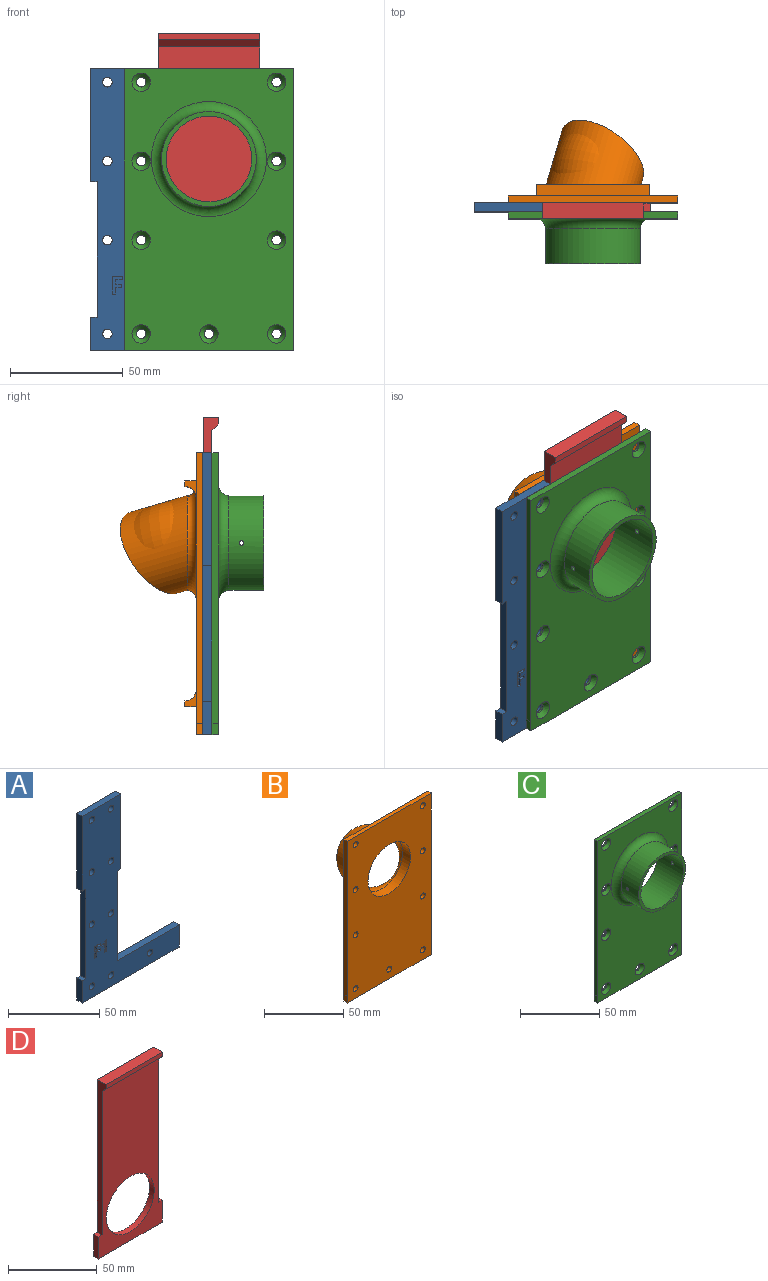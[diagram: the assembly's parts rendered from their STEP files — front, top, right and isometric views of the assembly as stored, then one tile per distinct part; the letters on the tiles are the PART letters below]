
ASSEMBLY  parts=4 mates=3
PART A: 45 faces, bbox 75x4x125 mm
  f0: plane 125x75mm, normal (0,-1,0), area 3900.4mm2, adj f1,f2,f3,f4,f5,f6,f7,f8
  f1: plane 30x4mm, normal (0,0,1), area 120mm2, adj f0,f2,f12,f17
  f2: plane 50.1x4mm, normal (-1,0,0), area 200.4mm2, adj f0,f1,f3,f12
  f3: plane 4x3mm, normal (0,0,-1), area 12mm2, adj f0,f2,f4,f12
  f4: plane 60x4mm, normal (-1,0,0), area 240mm2, adj f0,f3,f5,f12
  f5: plane 4x3mm, normal (0,0,1), area 12mm2, adj f0,f4,f6,f12
  f6: plane 14.9x4mm, normal (-1,0,0), area 59.6mm2, adj f0,f5,f11,f12
  f7: cylinder r=2.1mm len=4.2mm, axis (0,-1,0), area 52.8mm2, adj f0,f12
  f8: cylinder r=2.1mm len=4.2mm, axis (0,-1,0), area 52.8mm2, adj f0,f12
  f9: cylinder r=2.1mm len=4.2mm, axis (0,-1,0), area 52.8mm2, adj f0,f12
  f10: cylinder r=2.1mm len=4.2mm, axis (0,-1,0), area 52.8mm2, adj f0,f12
  f11: plane 75x4mm, normal (0,0,-1), area 300mm2, adj f0,f6,f12,f13
  f12: plane 125x75mm, normal (0,1,0), area 3935.9mm2, adj f1,f2,f3,f4,f5,f6,f7,f8
  f13: plane 14.9x4mm, normal (1,0,0), area 59.6mm2, adj f0,f11,f12,f14
  f14: plane 48x4mm, normal (0,0,1), area 192mm2, adj f0,f12,f13,f15
  f15: plane 60x4mm, normal (1,0,0), area 240mm2, adj f0,f12,f14,f16
  f16: plane 4x3mm, normal (0,0,-1), area 12mm2, adj f0,f12,f15,f17
  f17: plane 50.1x4mm, normal (1,0,0), area 200.4mm2, adj f0,f1,f12,f16
  f18: cylinder r=2.1mm len=4.2mm, axis (0,-1,0), area 52.8mm2, adj f0,f12
  f19: cylinder r=2.1mm len=4.2mm, axis (0,-1,0), area 52.8mm2, adj f0,f12
  f20: cylinder r=2.1mm len=4.2mm, axis (0,-1,0), area 52.8mm2, adj f0,f12
  f21: cylinder r=2.1mm len=4.2mm, axis (0,-1,0), area 52.8mm2, adj f0,f12
  f22: cylinder r=2.1mm len=4.2mm, axis (0,-1,0), area 52.8mm2, adj f0,f12
  f23: plane 1.64x1mm, normal (0,0,1), area 1.6mm2, adj f0,f24,f32,f33
  f24: plane 7.76x1mm, normal (-1,0,0), area 7.8mm2, adj f0,f23,f25,f33
  f25: plane 1.35x1mm, normal (0,0,-1), area 1.3mm2, adj f0,f24,f26,f33
  f26: plane 2.5x1.99mm, normal (0.62,0,-0.78), area 3.2mm2, adj f0,f25,f27,f33
  f27: plane 1x0.99mm, normal (0.78,0,0.63), area 1.3mm2, adj f0,f26,f28,f33
  f28: plane 1x0.89mm, normal (-0.63,0,0.78), area 1.1mm2, adj f0,f27,f29,f33
  f29: extruded ~1x0.57mm, area 0.8mm2, adj f0,f28,f30,f33
  f30: plane 1x0.81mm, normal (1,0,-0.03), area 0.8mm2, adj f0,f29,f31,f33
  f31: plane 1x0.74mm, normal (1,0,-0.02), area 0.7mm2, adj f0,f30,f32,f33
  f32: plane 4.49x1mm, normal (1,0,0), area 4.5mm2, adj f0,f23,f31,f33
  f33: plane 7.76x3.85mm, normal (0,-1,0), area 15.6mm2, adj f23,f24,f25,f26,f27,f28,f29,f30
  f34: plane 1.62x1mm, normal (0,0,1), area 1.6mm2, adj f0,f35,f43,f44
  f35: plane 3.07x1mm, normal (-1,0,0), area 3.1mm2, adj f0,f34,f36,f44
  f36: plane 2.63x1mm, normal (0,0,1), area 2.6mm2, adj f0,f35,f37,f44
  f37: plane 1.34x1mm, normal (-1,0,0), area 1.3mm2, adj f0,f36,f38,f44
  f38: plane 2.63x1mm, normal (0,0,-1), area 2.6mm2, adj f0,f37,f39,f44
  f39: plane 2x1mm, normal (-1,0,0), area 2mm2, adj f0,f38,f40,f44
  f40: plane 2.83x1mm, normal (0,0,1), area 2.8mm2, adj f0,f39,f41,f44
  f41: plane 1.35x1mm, normal (-1,0,0), area 1.3mm2, adj f0,f40,f42,f44
  f42: plane 4.45x1mm, normal (0,0,-1), area 4.4mm2, adj f0,f41,f43,f44
  f43: plane 7.76x1mm, normal (1,0,0), area 7.8mm2, adj f0,f34,f42,f44
  f44: plane 7.76x4.45mm, normal (0,-1,0), area 19.9mm2, adj f34,f35,f36,f37,f38,f39,f40,f41
PART B: 35 faces, bbox 75x39.1x125 mm
  f0: plane 125x75mm, normal (0,1,0), area 6638.9mm2, adj f1,f2,f3,f4,f5,f6,f7,f8
  f1: plane 125x3mm, normal (1,0,0), area 375mm2, adj f0,f2,f13,f15
  f2: plane 75x3mm, normal (0,0,1), area 225mm2, adj f0,f1,f3,f15
  f3: plane 120x3mm, normal (-1,0,0), area 360mm2, adj f0,f2,f4,f15
  f4: plane 5x3mm, normal (-1,0,0), area 15mm2, adj f0,f3,f13,f15
  f5: cylinder r=2.1mm len=4.2mm, axis (0,-1,0), area 39.6mm2, adj f0,f15
  f6: cylinder r=2.1mm len=4.2mm, axis (0,-1,0), area 39.6mm2, adj f0,f15
  f7: cylinder r=2.1mm len=4.2mm, axis (0,-1,0), area 39.6mm2, adj f0,f15
  f8: cylinder r=2.1mm len=4.2mm, axis (0,-1,0), area 39.6mm2, adj f0,f15
  f9: cylinder r=2.1mm len=4.2mm, axis (0,-1,0), area 39.6mm2, adj f0,f15
  f10: cylinder r=2.1mm len=4.2mm, axis (0,-1,0), area 39.6mm2, adj f0,f15
  f11: cylinder r=2.1mm len=4.2mm, axis (0,-1,0), area 39.6mm2, adj f0,f15
  f12: cylinder r=2.1mm len=4.2mm, axis (0,-1,0), area 39.6mm2, adj f0,f15
  f13: plane 75x3mm, normal (0,0,-1), area 225mm2, adj f0,f1,f4,f15
  f14: cylinder r=2.1mm len=4.2mm, axis (0,-1,0), area 39.6mm2, adj f0,f15
  f15: plane 125x75mm, normal (0,-1,0), area 8116.1mm2, adj f1,f2,f3,f4,f5,f6,f7,f8
  f16: cylinder r=19mm len=38mm, axis (0,-1,0), area 835.7mm2, adj f15,f18
  f17: torus R=21mm, axis (0.71,0,0.71), area 2176.2mm2, adj f19,f29
  f18: torus R=21mm, axis (0.71,0,0.71), area 1969mm2, adj f16,f19
  f19: plane 36.37x36.37mm, normal (0.5,0.71,-0.5), area 251.3mm2, adj f17,f18
  f20: plane 7.5x5mm, normal (1,0,0), area 17.9mm2, adj f0,f23,f24,f30
  f21: plane 30.01x5mm, normal (0,0,-1), area 56.4mm2, adj f24,f31,f33
  f22: plane 7.5x5mm, normal (-1,0,0), area 17.9mm2, adj f0,f23,f24,f34
  f23: plane 50x5mm, normal (0,0,1), area 250mm2, adj f0,f20,f22,f24
  f24: plane 50x2.5mm, normal (0,1,0), area 125mm2, adj f20,f21,f22,f23,f30,f34
  f25: plane 7.5x5mm, normal (1,0,0), area 17.9mm2, adj f0,f26,f28,f32
  f26: plane 50x5mm, normal (0,0,-1), area 250mm2, adj f0,f25,f27,f28
  f27: plane 7.5x5mm, normal (-1,0,0), area 17.9mm2, adj f0,f26,f28,f32
  f28: plane 50x2.5mm, normal (0,1,0), area 125mm2, adj f25,f26,f27,f32
  f29: torus R=25mm, axis (0,-1,0), area 886.4mm2, adj f0,f17,f31,f33
  f30: cylinder r=5mm len=10mm, axis (1,0,0), area 78.5mm2, adj f0,f20,f24,f31
  f31: bspline ~15.34x5.19mm, area 56.4mm2, adj f21,f29,f30
  f32: cylinder r=5mm len=50mm, axis (-1,0,0), area 392.7mm2, adj f0,f25,f27,f28
  f33: bspline ~15.34x5.19mm, area 56.4mm2, adj f21,f29,f34
  f34: cylinder r=5mm len=10mm, axis (1,0,0), area 78.5mm2, adj f0,f22,f24,f33
PART C: 31 faces, bbox 75x23x125 mm
  f0: plane 125x3mm, normal (1,0,0), area 375mm2, adj f1,f13,f15,f16
  f1: plane 75x3mm, normal (0,0,1), area 225mm2, adj f0,f2,f15,f16
  f2: plane 120x3mm, normal (-1,0,0), area 360mm2, adj f1,f3,f15,f16
  f3: plane 5x3mm, normal (-1,0,0), area 15mm2, adj f2,f13,f15,f16
  f4: cylinder r=2.1mm len=4.2mm, axis (0,-1,0), area 13.2mm2, adj f15,f22
  f5: cylinder r=2.1mm len=4.2mm, axis (0,-1,0), area 13.2mm2, adj f15,f23
  f6: cylinder r=2.1mm len=4.2mm, axis (0,-1,0), area 13.2mm2, adj f15,f24
  f7: cylinder r=2.1mm len=4.2mm, axis (0,-1,0), area 13.2mm2, adj f15,f25
  f8: cylinder r=2.1mm len=4.2mm, axis (0,-1,0), area 13.2mm2, adj f15,f26
  f9: cylinder r=2.1mm len=4.2mm, axis (0,-1,0), area 13.2mm2, adj f15,f27
  f10: cylinder r=2.1mm len=4.2mm, axis (0,-1,0), area 13.2mm2, adj f15,f28
  f11: cylinder r=2.1mm len=4.2mm, axis (0,-1,0), area 13.2mm2, adj f15,f29
  f12: cylinder r=2.1mm len=4.2mm, axis (0,-1,0), area 13.2mm2, adj f15,f30
  f13: plane 75x3mm, normal (0,0,-1), area 225mm2, adj f0,f3,f15,f16
  f14: cylinder r=19mm len=38mm, axis (0,-1,0), area 2739.4mm2, adj f15,f18,f20,f21
  f15: plane 125x75mm, normal (0,1,0), area 8116.1mm2, adj f0,f1,f2,f3,f4,f5,f6,f7
  f16: plane 125x75mm, normal (0,-1,0), area 6856.8mm2, adj f0,f1,f2,f3,f13,f19,f22,f23
  f17: cylinder r=21mm len=42mm, axis (0,1,0), area 2038.9mm2, adj f18,f19,f20,f21
  f18: plane 42x42mm, normal (0,-1,0), area 251.3mm2, adj f14,f17
  f19: torus R=25.5mm, axis (0,-1,0), area 1005.3mm2, adj f16,f17
  f20: cylinder r=1mm len=2.03mm, axis (1,0,0), area 12.6mm2, adj f14,f17
  f21: cylinder r=1mm len=2.03mm, axis (1,0,0), area 12.6mm2, adj f14,f17
  f22: cone r=2.1mm half-angle=45deg, axis (0,-1,0), area 55.1mm2, adj f4,f16
  f23: cone r=2.1mm half-angle=45deg, axis (0,-1,0), area 55.1mm2, adj f5,f16
  f24: cone r=2.1mm half-angle=45deg, axis (0,-1,0), area 55.1mm2, adj f6,f16
  f25: cone r=2.1mm half-angle=45deg, axis (0,-1,0), area 55.1mm2, adj f7,f16
  f26: cone r=2.1mm half-angle=45deg, axis (0,-1,0), area 55.1mm2, adj f8,f16
  f27: cone r=2.1mm half-angle=45deg, axis (0,-1,0), area 55.1mm2, adj f9,f16
  f28: cone r=2.1mm half-angle=45deg, axis (0,-1,0), area 55.1mm2, adj f10,f16
  f29: cone r=2.1mm half-angle=45deg, axis (0,-1,0), area 55.1mm2, adj f11,f16
  f30: cone r=2.1mm half-angle=45deg, axis (0,-1,0), area 55.1mm2, adj f12,f16
PART D: 14 faces, bbox 50.8x6.9x120.1 mm
  f0: plane 114x50.8mm, normal (0,-1,0), area 4063.7mm2, adj f1,f2,f3,f4,f5,f6,f7,f8
  f1: plane 105x6.9mm, normal (-1,0,0), area 413.1mm2, adj f0,f2,f9,f11,f12,f13
  f2: plane 3.8x3mm, normal (0,0,1), area 11.4mm2, adj f0,f1,f3,f11
  f3: plane 15.1x3.8mm, normal (-1,0,0), area 57.4mm2, adj f0,f2,f4,f11
  f4: plane 50.8x3.8mm, normal (0,0,-1), area 193mm2, adj f0,f3,f5,f11
  f5: plane 15.1x3.8mm, normal (1,0,0), area 57.4mm2, adj f0,f4,f6,f11
  f6: plane 3.8x3mm, normal (0,0,1), area 11.4mm2, adj f0,f5,f7,f11
  f7: plane 95x3.8mm, normal (1,0,0), area 361mm2, adj f0,f6,f8,f11
  f8: plane 10x6.9mm, normal (1,0,0), area 52.1mm2, adj f0,f7,f9,f11,f12,f13
  f9: plane 44.8x6.9mm, normal (0,0,1), area 309.1mm2, adj f1,f8,f11,f12
  f10: cylinder r=19mm len=38mm, axis (0,-1,0), area 453.6mm2, adj f0,f11
  f11: plane 120.1x50.8mm, normal (0,1,0), area 4337mm2, adj f1,f2,f3,f4,f5,f6,f7,f8
  f12: plane 44.8x3mm, normal (0,-1,0), area 134.4mm2, adj f1,f8,f9,f13
  f13: plane 44.8x3.1mm, normal (0,-0.71,-0.71), area 196.4mm2, adj f0,f1,f8,f12
PLACE A rot(axis=(0,0,-1),0deg) t=(-2.12,1.57,-31.55)mm
PLACE B rot(axis=(0,0,-1),0deg) t=(-2.12,1.57,-31.55)mm fixed
PLACE C rot(axis=(0,0,-1),0deg) t=(-2.12,1.57,-31.55)mm
PLACE D t=(-2.02,1.57,-25.8)mm
MATE fastened C.f8 <-> A.f22  axis (0,1,0) through (-2.12,4.57,-114.05)mm
MATE slider A.f14 <-> D.f4  axis (0,0,1) through (-3.62,6.57,-106.65)mm
MATE fastened A.f22 <-> B.f14  axis (0,1,0) through (-2.12,8.57,-114.05)mm
